# Revit family: 6280 series
name_source: partatom
category: Mechanical Equipment
revit_build: Autodesk Revit 2013 (Build: 20120221_2030(x64)
units: mm (PartAtom-declared; Revit-internal decimal feet)

## types (4) — shared parameters
Assembly Code = D2010900
Default Elevation = 0"
Description = Commercial Sewage Pumps
Discharge Height = 6 1/4"
Height = 21 7/16"
Hertz = 60
Impeller Type = Cast Iron Vortex
Installation Type = Floor Mounted
Insulation = Class B
Lead Wires Insulation = Class B
Length = 13 9/16"
Manufacturer = Zoeller
Masterformat Number = 33 36 16
Masterformat Title = Utility Septic Tank Effluent Pumps
Material = Cast Iron-Zoeller-Powder Coated Epoxy
Max. Stator Temp. = 266 °F
Max. Water Temp. = 130 °F
Min. Recommended Fluid Level = 10"
Minimum Head = 60"
Moisture Sensor (Optional) = Requires a circuit in control panel
Motor Design Letter = NEMA B
Motor Shaft = 416 S.S.
Motor Thermal Shutoff (Single Phase Only) = Thermal Overload Protector With Automatic Reset.
Motor Type = Submersible
O-Rings and Cover Gasket = Viton
Omniclass Table 23 Code = 23.60.30.21
Omniclass Table 23 Title = Pumps
Operation = Non-Automatic
Phase = 1 or 3
Price = Prices may vary. Please consult Manufacturer Representative for most up-to-date price list.
Product Page URL = http://www.zoellerengprod.com
RPM = 1750
Service Factor = 1.15
Shaft Seal Lower (Options) = Silicon Carbide/Silicon Carbide
Shaft Seal Lower Standard = Silicon Carbide/Carbon
Shaft Seal Upper (Options) = Silicon Carbide/Carbon, Silicon Carbide/Silicon Carbide
Shaft Seal Upper Standard = Carbon/Ceramic
Shipping Weight = 89 lbs
Type = Permanent Split Capacitor or 3 Phase
Type SOW Power Cord Length = 300"
URL = http://www.zoellerengprod.com
Warranty Information = 36 Months (Limited)
Waste Connection = Yes
Width = 10"

## per-type parameters (varying)
| type | Discharge Diameter | Discharge Radius | Full Load Amps (Voltage Dependent) | Locked Rotor Amps (Voltage Dependant) | Max. Flow at Min. Head | Maximum Head | Motor | Voltage |
| 6282-2" | 2" NPT | 1" | 1.4 - 10.3 | 5.1 - 27.0 | 127 GPM @ 5' | 312" | 1/2 HP | 115-575 |
| 6282-3" | 3" NPT | 1 1/2" | 1.4 - 10.3 | 5.1 - 27.0 | 127 GPM @ 5' | 312" | 1/2 HP | 115-575 |
| 6284-2" | 2" NPT | 1" | 2.2 - 9.3 | 9.0 - 24.0 | 179 GPM @ 5' | 420" | 1 HP | 200-575 |
| 6284-3" | 3" NPT | 1 1/2" | 2.2 - 9.3 | 9.0 - 24.0 | 179 GPM @ 5' | 420" | 1 HP | 200-575 |

note: column(s) folded — value = type name in every type: Model

## geometry (parser evidence)
native form markers: Blend x4, Sweep x1
no freeform markers — native parametric forms only
